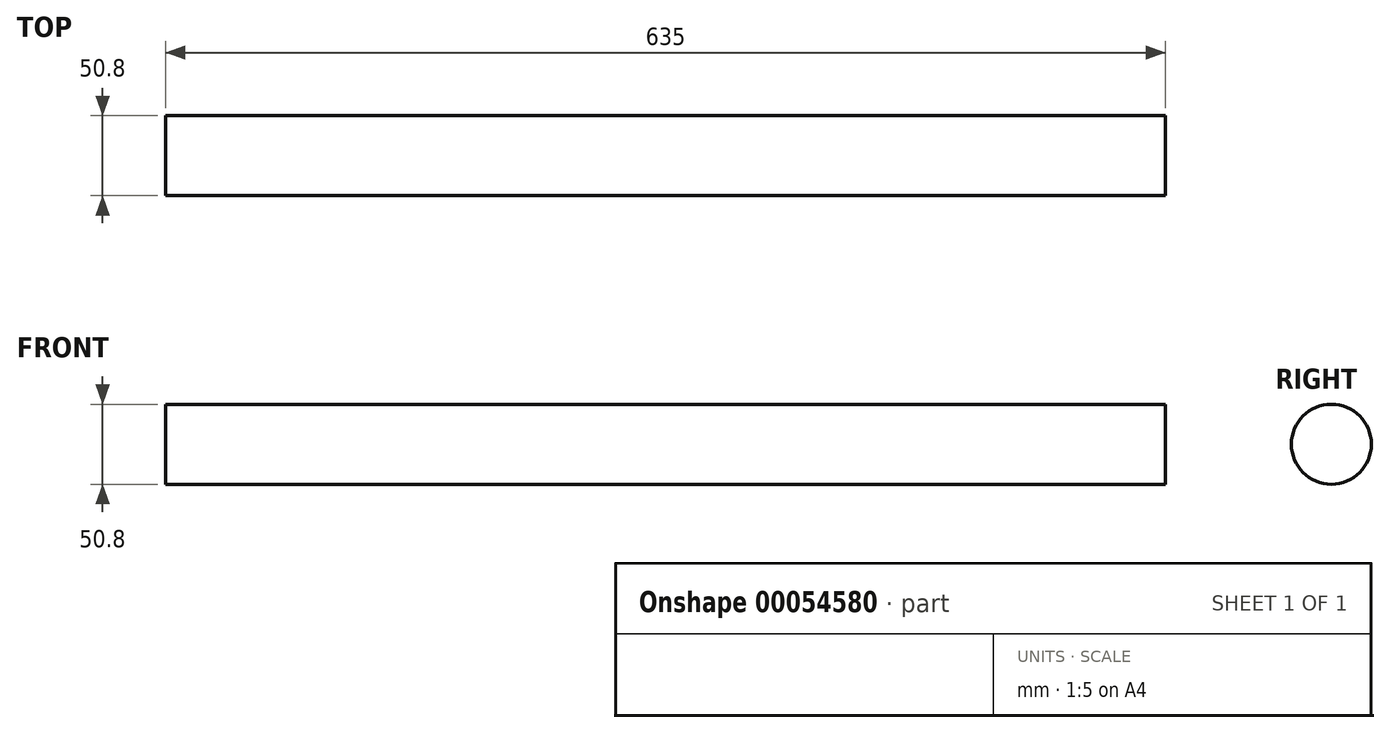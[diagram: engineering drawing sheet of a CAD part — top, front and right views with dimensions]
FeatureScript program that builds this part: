
annotation { "Feature Type Name" : "Feature", "Feature Type Description" : "" }
export const myFeature = defineFeature(function(context is Context, id is Id, definition is map)
    precondition{}
    {
        {
            var Q0;
            Q0=qCreatedBy(makeId("Right.planeOp"),FACE);
            var sketch = newSketch(context, id + "F0", { "sketchPlane" : qUnion([Q0])});
            skCircle(sketch, "E0", {"center": v(0, 0) * mm, "radius": 25.4 * mm});
            skSolve(sketch);
        }
        {
            var Q0;
            Q0=qCreatedBy(makeId("Front.planeOp"),FACE);
            var sketch = newSketch(context, id + "F1", { "sketchPlane" : qUnion([Q0])});
            skLineSegment(sketch, "E1", {"start": v(0, 0) * mm, "end": v(-635, 0) * mm});
            skSolve(sketch);
        }
        {
            var Q0;
            Q0 = qSketchRegion(id + "F0", true);
            var Q1;
            Q1 = qConstructionFilter(qBodyType(qCreatedBy(id + "F1" ,EDGE), BodyType.WIRE), ConstructionObject.NO);
            sweep(context, id + "F2", {"profiles" : qUnion([Q0]), "path" : qUnion([Q1])});
        }
        {
            var Q0;
            Q0=qCreatedBy(makeId("Front.planeOp"),FACE);
            var sketch = newSketch(context, id + "F3", { "sketchPlane" : qUnion([Q0])});
            skLineSegment(sketch, "E2", {"start": v(-50.8, 0) * mm, "end": v(-94.8, 76.2) * mm});
            skLineSegment(sketch, "E3", {"start": v(-94.8, 76.2) * mm, "end": v(-540.2, 76.2) * mm});
            skLineSegment(sketch, "E4", {"start": v(-540.2, 76.2) * mm, "end": v(-584.2, 0) * mm});
            skSolve(sketch);
        }
    });
